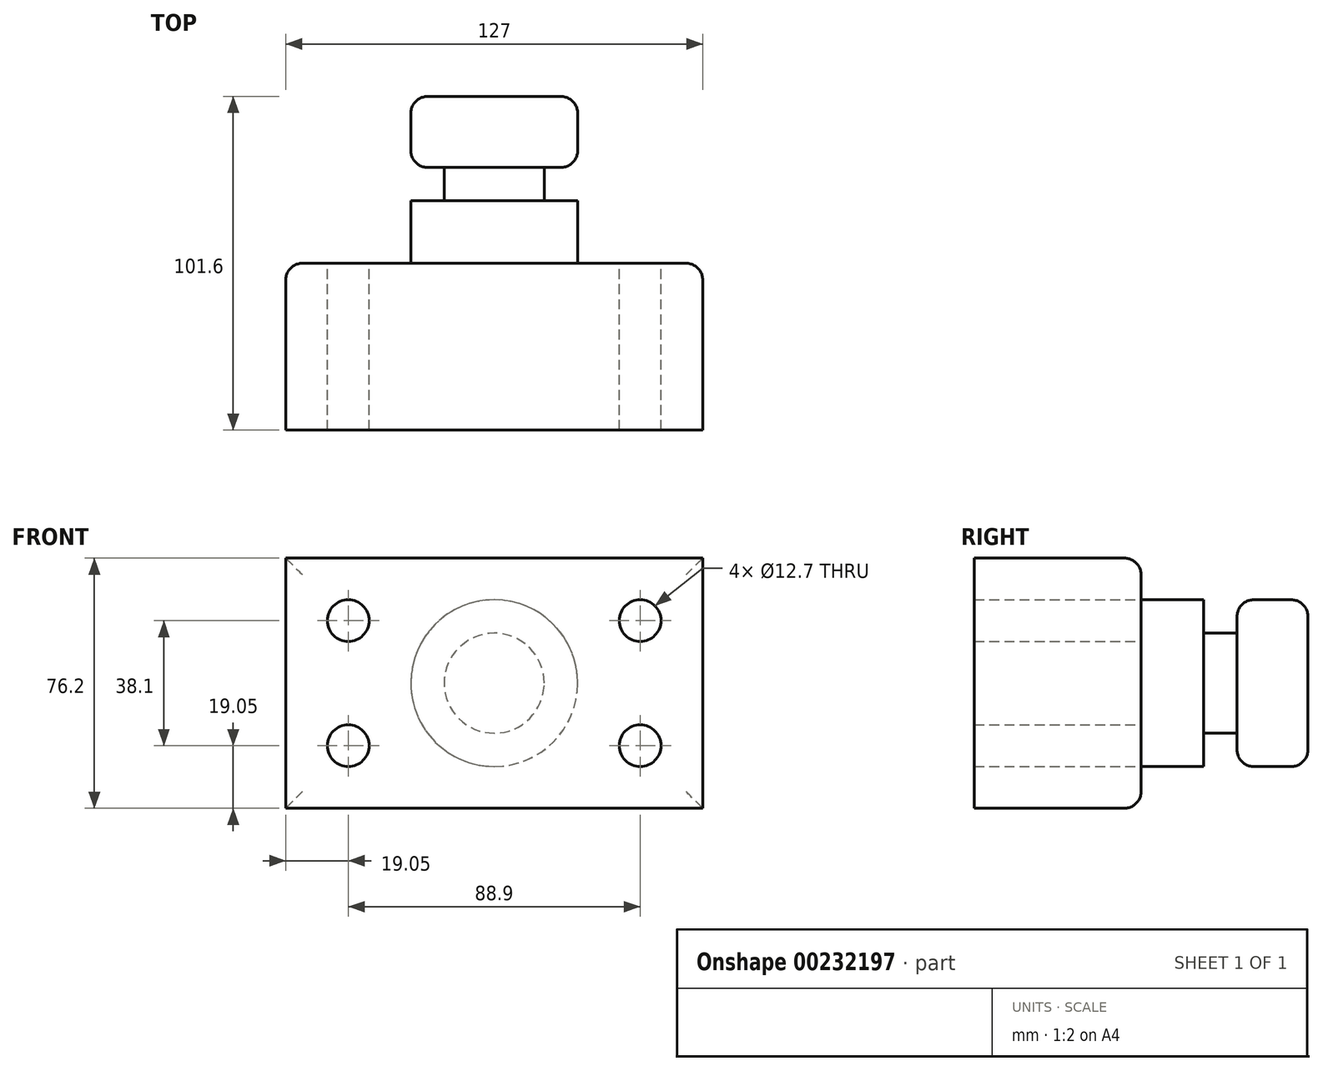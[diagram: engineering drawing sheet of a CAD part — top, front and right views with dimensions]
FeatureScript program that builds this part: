
annotation { "Feature Type Name" : "Feature", "Feature Type Description" : "" }
export const myFeature = defineFeature(function(context is Context, id is Id, definition is map)
    precondition{}
    {
        {
            var Q0;
            Q0=qCreatedBy(makeId("Front.planeOp"),FACE);
            var sketch = newSketch(context, id + "F0", { "sketchPlane" : qUnion([Q0])});
            skLineSegment(sketch, "E0.bottom", {"start": v(-63.5, -38.1) * mm, "end": v(63.5, -38.1) * mm});
            skLineSegment(sketch, "E0.top", {"start": v(-63.5, 38.1) * mm, "end": v(63.5, 38.1) * mm});
            skLineSegment(sketch, "E0.left", {"start": v(-63.5, -38.1) * mm, "end": v(-63.5, 38.1) * mm});
            skLineSegment(sketch, "E0.right", {"start": v(63.5, -38.1) * mm, "end": v(63.5, 38.1) * mm});
            skPoint(sketch, "E0.middle", {"position": v(0, 0) * mm});
            skCircle(sketch, "E1", {"center": v(-44.45, 19.05) * mm, "radius": 6.35 * mm});
            skCircle(sketch, "E2", {"center": v(44.45, 19.05) * mm, "radius": 6.35 * mm});
            skCircle(sketch, "E3", {"center": v(44.45, -19.05) * mm, "radius": 6.35 * mm});
            skCircle(sketch, "E4", {"center": v(-44.45, -19.05) * mm, "radius": 6.35 * mm});
            skSolve(sketch);
        }
        {
            var Q0;
            Q0=makeQuery(id+"F0.imprint","IMPRINT",FACE,{"disambiguationData":[TD([[makeQuery(id+"F0.imprint","IMPRINT",EDGE,{"derivedFrom":sQuery(id+"F0.wireOp",EDGE,"E0.bottom")}),1.0]])]});
            extrude(context, id + "F1", {"entities" : qUnion([Q0]), "depth" : 50.8 * mm});
        }
        {
            var Q0;
            Q0=makeQuery(id+"F1.opExtrude","CAP_FACE",FACE,{"disambiguationData":[OSD([sQuery(id+"F0.wireOp",EDGE,"E0.bottom"),sQuery(id+"F0.wireOp",EDGE,"E0.top"),sQuery(id+"F0.wireOp",EDGE,"E0.left"),sQuery(id+"F0.wireOp",EDGE,"E0.right"),sQuery(id+"F0.wireOp",EDGE,"E1"),sQuery(id+"F0.wireOp",EDGE,"E2"),sQuery(id+"F0.wireOp",EDGE,"E3"),sQuery(id+"F0.wireOp",EDGE,"E4")])],"isStart":true});
            var sketch = newSketch(context, id + "F2", { "sketchPlane" : qUnion([Q0])});
            skCircle(sketch, "E5", {"center": v(0, 0) * mm, "radius": 25.4 * mm});
            skSolve(sketch);
        }
        {
            var Q0;
            Q0=qCreatedBy(makeId("Right.planeOp"),FACE);
            var sketch = newSketch(context, id + "F3", { "sketchPlane" : qUnion([Q0])});
            skLineSegment(sketch, "E6.bottom", {"start": v(0, 0) * mm, "end": v(50.8, 0) * mm});
            skLineSegment(sketch, "E6.top", {"start": v(0, -25.4) * mm, "end": v(50.8, -25.4) * mm});
            skLineSegment(sketch, "E6.left", {"start": v(0, 0) * mm, "end": v(0, -25.4) * mm});
            skLineSegment(sketch, "E6.right", {"start": v(50.8, 0) * mm, "end": v(50.8, -25.4) * mm});
            skSolve(sketch);
        }
        {
            var Q0;
            Q0=makeQuery(id+"F3.imprint","IMPRINT",FACE,{"disambiguationData":[TD([[makeQuery(id+"F3.imprint","IMPRINT",EDGE,{"derivedFrom":sQuery(id+"F3.wireOp",EDGE,"E6.bottom")}),-1.0]])]});
            var Q1;
            Q1=sQuery(id+"F3.wireOp",EDGE,"E6.bottom");
            revolve(context, id + "F4", {"operationType" : NewBodyOperationType.ADD, "entities" : qUnion([Q0]), "axis" : qUnion([Q1]), "revolveType" : RevolveType.FULL});
        }
        {
            var Q0;
            Q0=qCreatedBy(makeId("Right.planeOp"),FACE);
            var sketch = newSketch(context, id + "F5", { "sketchPlane" : qUnion([Q0])});
            skLineSegment(sketch, "E7.bottom", {"start": v(19.05, 25.4) * mm, "end": v(29.21, 25.4) * mm});
            skLineSegment(sketch, "E7.top", {"start": v(19.05, 15.24) * mm, "end": v(29.21, 15.24) * mm});
            skLineSegment(sketch, "E7.left", {"start": v(19.05, 25.4) * mm, "end": v(19.05, 15.24) * mm});
            skLineSegment(sketch, "E7.right", {"start": v(29.21, 25.4) * mm, "end": v(29.21, 15.24) * mm});
            skLineSegment(sketch, "E8", {"start": v(0, 0) * mm, "end": v(76.73, 0) * mm});
            skSolve(sketch);
        }
        {
            var Q0;
            Q0 = qSketchRegion(id + "F5", true);
            var Q1;
            Q1=sQuery(id+"F5.wireOp",EDGE,"E8");
            revolve(context, id + "F6", {"operationType" : NewBodyOperationType.REMOVE, "entities" : qUnion([Q0]), "axis" : qUnion([Q1]), "revolveType" : RevolveType.FULL, "oppositeDirection" : true});
        }
        {
            var Q0;
            Q0=makeQuery(id+"F1.opExtrude","CAP_EDGE",EDGE,{"disambiguationData":[OSD([sQuery(id+"F0.wireOp",EDGE,"E0.right")])],"isStart":true});
            var Q1;
            Q1=makeQuery(id+"F1.opExtrude","CAP_EDGE",EDGE,{"disambiguationData":[OSD([sQuery(id+"F0.wireOp",EDGE,"E0.top")])],"isStart":true});
            var Q2;
            Q2=makeQuery(id+"F1.opExtrude","CAP_EDGE",EDGE,{"disambiguationData":[OSD([sQuery(id+"F0.wireOp",EDGE,"E0.bottom")])],"isStart":true});
            var Q3;
            Q3=makeQuery(id+"F1.opExtrude","CAP_EDGE",EDGE,{"disambiguationData":[OSD([sQuery(id+"F0.wireOp",EDGE,"E0.left")])],"isStart":true});
            var Q4;
            Q4=makeQuery(id+"F6.boolean.opBoolean","COPY",EDGE,{"derivedFrom":makeQuery(id+"F6.opRevolve","SWEPT_EDGE",EDGE,{"disambiguationData":[OSD([sQuery(id+"F5.wireOp",EDGE,"E7.bottom"),sQuery(id+"F5.wireOp",EDGE,"E7.left")])]})});
            var Q5;
            Q5=makeQuery(id+"F6.boolean.opBoolean","COPY",EDGE,{"derivedFrom":makeQuery(id+"F6.opRevolve","SWEPT_EDGE",EDGE,{"disambiguationData":[OSD([sQuery(id+"F5.wireOp",EDGE,"E7.bottom"),sQuery(id+"F5.wireOp",EDGE,"E7.right")])]})});
            var Q6;
            Q6=makeQuery(id+"F4.opRevolve","SWEPT_EDGE",EDGE,{"disambiguationData":[OSD([sQuery(id+"F3.wireOp",EDGE,"E6.top"),sQuery(id+"F3.wireOp",EDGE,"E6.right")])]});
            fillet(context, id + "F7", {"entities" : qUnion([Q0, Q1, Q2, Q3, Q4, Q5, Q6]), "radius" : 5.08 * mm, "tangentPropagation" : true, "allowEdgeOverflow" : false});
        }
    });
